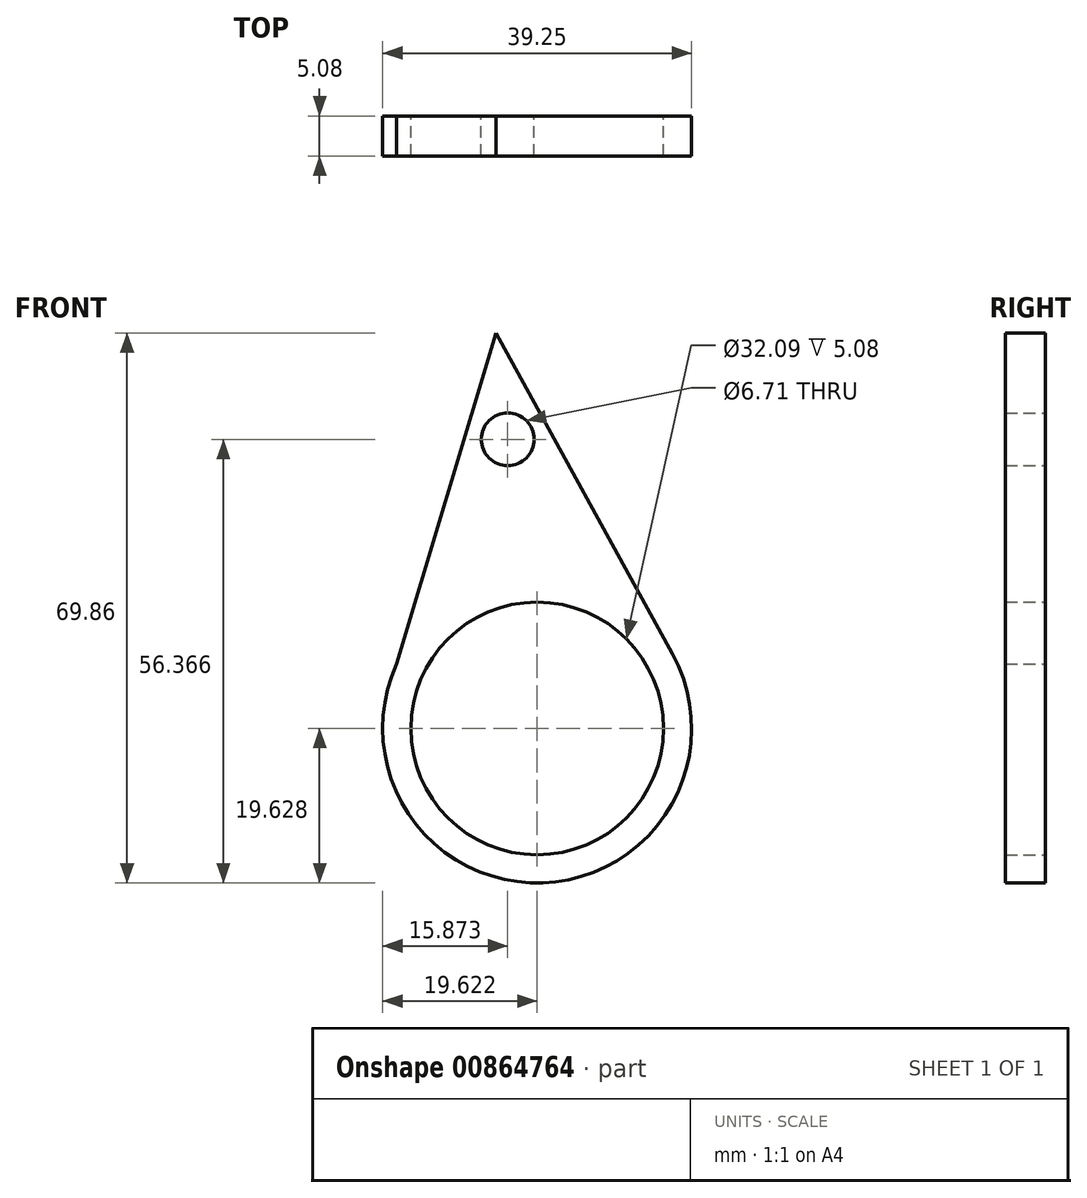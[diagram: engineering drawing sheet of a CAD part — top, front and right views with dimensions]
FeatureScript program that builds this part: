
annotation { "Feature Type Name" : "Feature", "Feature Type Description" : "" }
export const myFeature = defineFeature(function(context is Context, id is Id, definition is map)
    precondition{}
    {
        {
            var Q0;
            Q0=qCreatedBy(makeId("Front.planeOp"),FACE);
            var sketch = newSketch(context, id + "F0", { "sketchPlane" : qUnion([Q0])});
            skArc(sketch, "E0", {"start": v(-268.24, -61.33) * mm, "mid": v(-249.67, -89.1) * mm, "end": v(-233.2, -60.03) * mm});
            skLineSegment(sketch, "E1", {"start": v(-269.8, -66.5) * mm, "end": v(-255.65, -19.26) * mm});
            skLineSegment(sketch, "E2", {"start": v(-255.65, -19.26) * mm, "end": v(-233.2, -60.03) * mm});
            skCircle(sketch, "E3", {"center": v(-254.15, -32.75) * mm, "radius": 3.35 * mm});
            skCircle(sketch, "E4", {"center": v(-250.4, -69.5) * mm, "radius": 16.05 * mm});
            skSolve(sketch);
        }
        {
            var Q0;
            Q0 = qSketchRegion(id + "F0", true);
            extrude(context, id + "F1", {"entities" : qUnion([Q0]), "depth" : 5.08 * mm, "offsetDistance" : 25.4 * mm});
        }
    });
